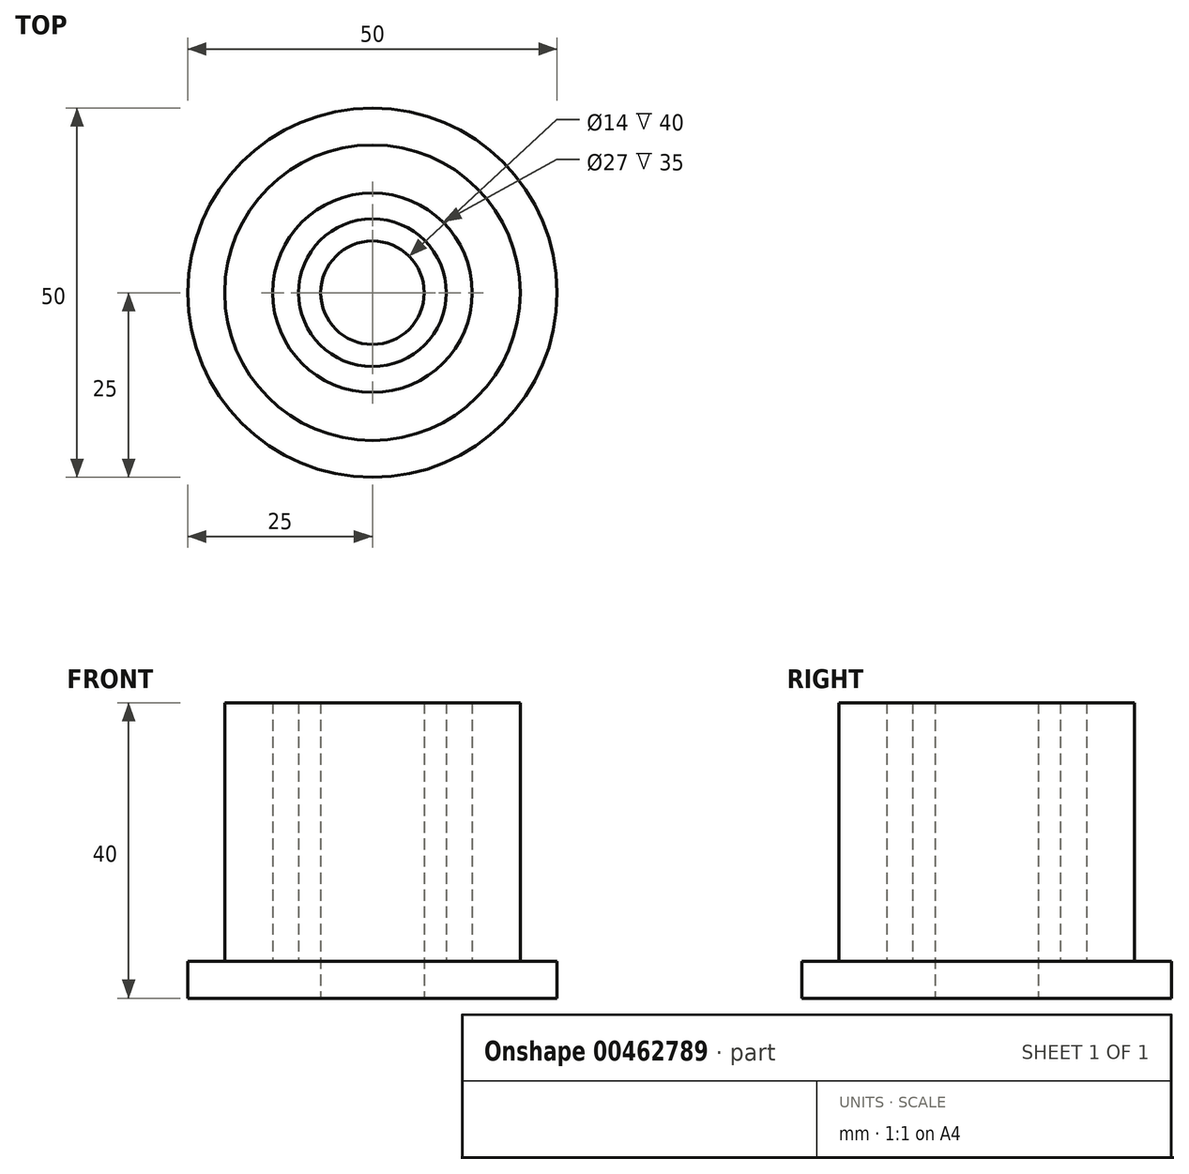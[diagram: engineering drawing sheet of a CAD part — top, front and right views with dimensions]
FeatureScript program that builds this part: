
annotation { "Feature Type Name" : "Feature", "Feature Type Description" : "" }
export const myFeature = defineFeature(function(context is Context, id is Id, definition is map)
    precondition{}
    {
        {
            var Q0;
            Q0=qCreatedBy(makeId("Top.planeOp"),FACE);
            var sketch = newSketch(context, id + "F0", { "sketchPlane" : qUnion([Q0])});
            skCircle(sketch, "E0", {"center": v(0, 0) * mm, "radius": 20 * mm});
            skCircle(sketch, "E1", {"center": v(0, 0) * mm, "radius": 25 * mm});
            skCircle(sketch, "E2", {"center": v(0, 0) * mm, "radius": 13.5 * mm});
            skCircle(sketch, "E3", {"center": v(0, 0) * mm, "radius": 10 * mm});
            skCircle(sketch, "E4", {"center": v(0, 0) * mm, "radius": 7 * mm});
            skSolve(sketch);
        }
        {
            var Q0;
            Q0=makeQuery(id+"F0.imprint","IMPRINT",FACE,{"disambiguationData":[TD([[makeQuery(id+"F0.imprint","IMPRINT",EDGE,{"derivedFrom":sQuery(id+"F0.wireOp",EDGE,"E0")}),-1.0]])]});
            var Q1;
            Q1=makeQuery(id+"F0.imprint","IMPRINT",FACE,{"disambiguationData":[TD([[makeQuery(id+"F0.imprint","IMPRINT",EDGE,{"derivedFrom":sQuery(id+"F0.wireOp",EDGE,"E0")}),1.0]])]});
            var Q2;
            Q2=makeQuery(id+"F0.imprint","IMPRINT",FACE,{"disambiguationData":[TD([[makeQuery(id+"F0.imprint","IMPRINT",EDGE,{"derivedFrom":sQuery(id+"F0.wireOp",EDGE,"E2")}),1.0]])]});
            var Q3;
            Q3=makeQuery(id+"F0.imprint","IMPRINT",FACE,{"disambiguationData":[TD([[makeQuery(id+"F0.imprint","IMPRINT",EDGE,{"derivedFrom":sQuery(id+"F0.wireOp",EDGE,"E3")}),1.0]])]});
            extrude(context, id + "F1", {"entities" : qUnion([Q0, Q1, Q2, Q3]), "depth" : 5 * mm});
        }
        {
            var Q0;
            Q0=makeQuery(id+"F0.imprint","IMPRINT",FACE,{"disambiguationData":[TD([[makeQuery(id+"F0.imprint","IMPRINT",EDGE,{"derivedFrom":sQuery(id+"F0.wireOp",EDGE,"E0")}),1.0]])]});
            extrude(context, id + "F2", {"entities" : qUnion([Q0]), "operationType" : NewBodyOperationType.ADD, "depth" : 40 * mm});
        }
        {
            var Q0;
            Q0=makeQuery(id+"F0.imprint","IMPRINT",FACE,{"disambiguationData":[TD([[makeQuery(id+"F0.imprint","IMPRINT",EDGE,{"derivedFrom":sQuery(id+"F0.wireOp",EDGE,"E3")}),1.0]])]});
            extrude(context, id + "F3", {"entities" : qUnion([Q0]), "operationType" : NewBodyOperationType.ADD, "depth" : 40 * mm});
        }
    });
